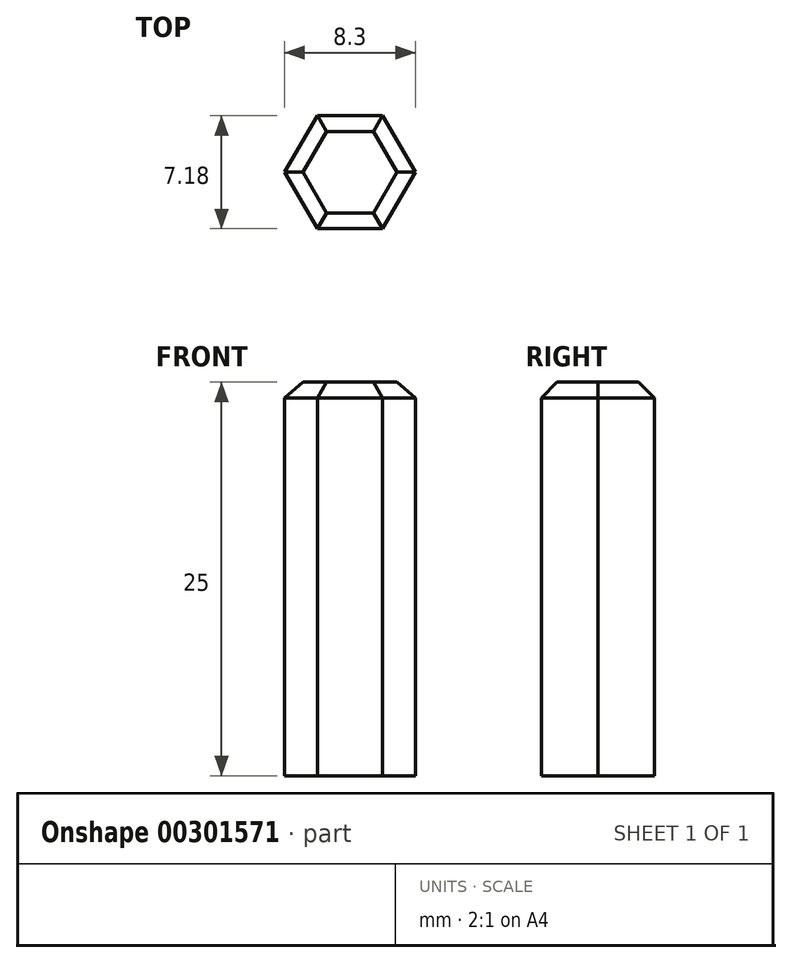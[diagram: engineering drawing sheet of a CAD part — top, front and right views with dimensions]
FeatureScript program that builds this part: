
annotation { "Feature Type Name" : "Feature", "Feature Type Description" : "" }
export const myFeature = defineFeature(function(context is Context, id is Id, definition is map)
    precondition{}
    {
        {
            var Q0;
            Q0=qCreatedBy(makeId("Top.planeOp"),FACE);
            var sketch = newSketch(context, id + "F0", { "sketchPlane" : qUnion([Q0])});
            skCircle(sketch, "E0.cCircle", {"center": v(0, 0) * mm, "radius": 3.6 * mm, "construction": true});
            skLineSegment(sketch, "E0.0", {"start": v(-4.15, 0) * mm, "end": v(-2.08, 3.6) * mm});
            skLineSegment(sketch, "E0.1", {"start": v(-2.08, 3.6) * mm, "end": v(2.08, 3.6) * mm});
            skLineSegment(sketch, "E0.2", {"start": v(2.08, 3.6) * mm, "end": v(4.15, 0) * mm});
            skLineSegment(sketch, "E0.3", {"start": v(4.15, 0) * mm, "end": v(2.08, -3.6) * mm});
            skLineSegment(sketch, "E0.4", {"start": v(2.08, -3.6) * mm, "end": v(-2.08, -3.6) * mm});
            skLineSegment(sketch, "E0.5", {"start": v(-2.08, -3.6) * mm, "end": v(-4.15, 0) * mm});
            skPoint(sketch, "E0.0.midPoint", {"position": v(-3.11, 1.8) * mm});
            skSolve(sketch);
        }
        {
            var Q0;
            Q0=qSketchRegion(id+"F0",true);
            extrude(context, id + "F1", {"entities" : qUnion([Q0]), "depth" : 25 * mm});
        }
        {
            var Q0;
            Q0=makeQuery(id+"F1.opExtrude","CAP_FACE",FACE,{"disambiguationData":[OSD([sQuery(id+"F0.wireOp",EDGE,"E0.0"),sQuery(id+"F0.wireOp",EDGE,"E0.1"),sQuery(id+"F0.wireOp",EDGE,"E0.2"),sQuery(id+"F0.wireOp",EDGE,"E0.3"),sQuery(id+"F0.wireOp",EDGE,"E0.4"),sQuery(id+"F0.wireOp",EDGE,"E0.5")])],"isStart":false});
            chamfer(context, id + "F2", {"entities" : qUnion([Q0]), "width" : 1 * mm, "tangentPropagation" : true});
        }
    });
